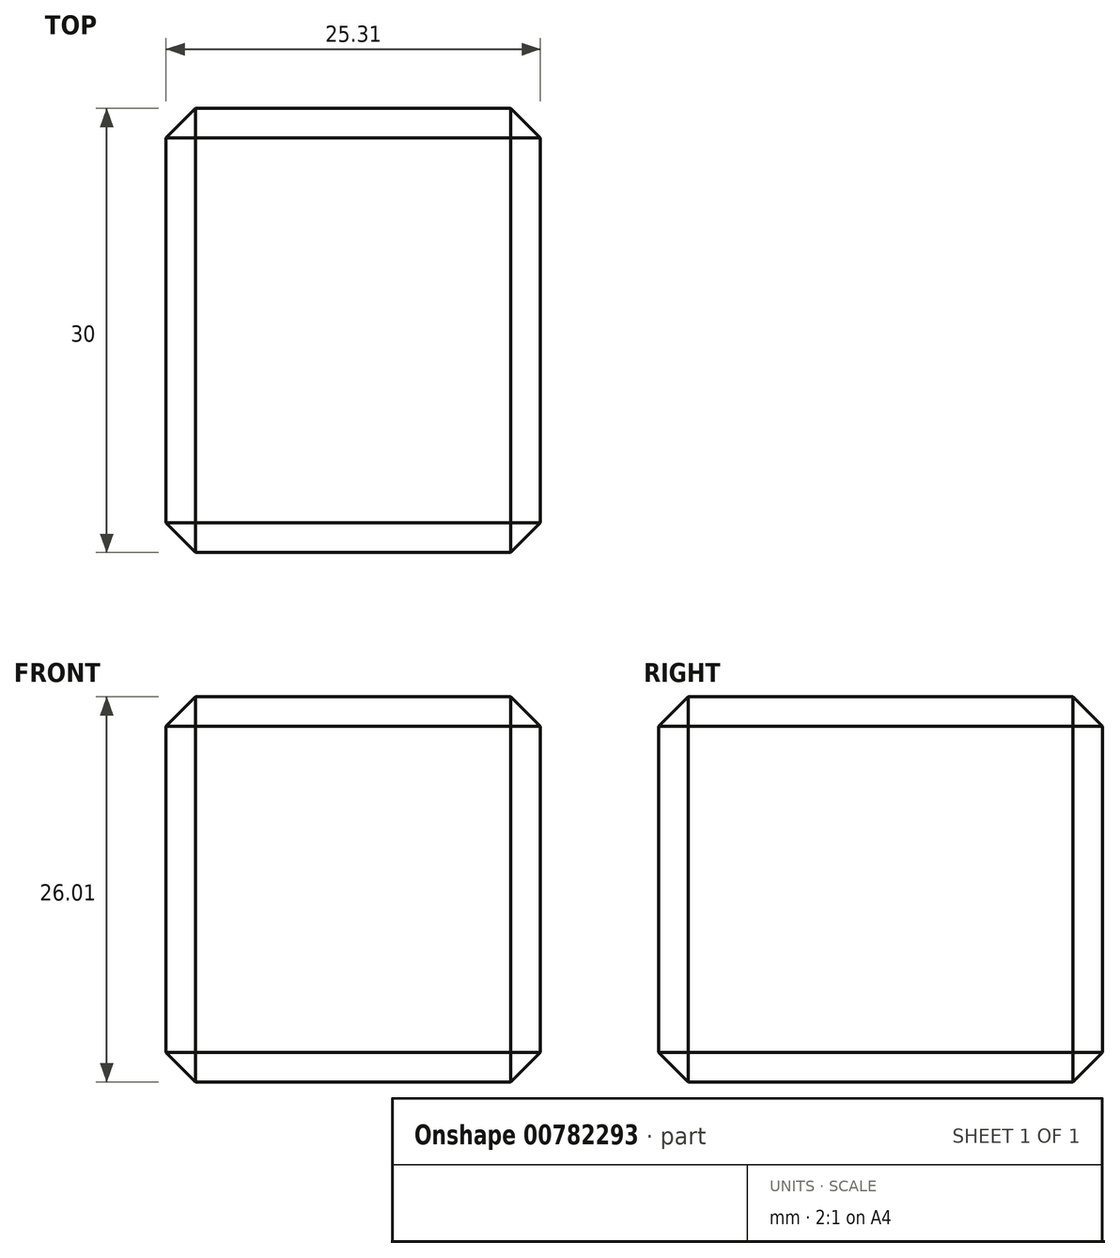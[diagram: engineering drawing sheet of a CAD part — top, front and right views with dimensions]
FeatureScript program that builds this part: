
annotation { "Feature Type Name" : "Feature", "Feature Type Description" : "" }
export const myFeature = defineFeature(function(context is Context, id is Id, definition is map)
    precondition{}
    {
        {
            var Q0;
            Q0=qCreatedBy(makeId("Front.planeOp"),FACE);
            var sketch = newSketch(context, id + "F0", { "sketchPlane" : qUnion([Q0])});
            skLineSegment(sketch, "E0.bottom", {"start": v(0, 0) * mm, "end": v(0, 0) * mm});
            skLineSegment(sketch, "E0.top", {"start": v(0, 0) * mm, "end": v(0, 0) * mm});
            skLineSegment(sketch, "E0.left", {"start": v(0, 0) * mm, "end": v(0, 0) * mm});
            skLineSegment(sketch, "E0.right", {"start": v(0, 0) * mm, "end": v(0, 0) * mm});
            skPoint(sketch, "E0.middle", {"position": v(0, 0) * mm});
            skLineSegment(sketch, "E1.bottom", {"start": v(0, 0) * mm, "end": v(25.31, 0) * mm});
            skLineSegment(sketch, "E1.top", {"start": v(0, 26.01) * mm, "end": v(25.31, 26.01) * mm});
            skLineSegment(sketch, "E1.left", {"start": v(0, 0) * mm, "end": v(0, 26.01) * mm});
            skLineSegment(sketch, "E1.right", {"start": v(25.31, 0) * mm, "end": v(25.31, 26.01) * mm});
            skPoint(sketch, "E1.middle", {"position": v(12.66, 13) * mm});
            skSolve(sketch);
        }
        {
            var Q0;
            Q0=makeQuery(id+"F0.imprint","IMPRINT",FACE,{"disambiguationData":[TD([[makeQuery(id+"F0.imprint","IMPRINT",EDGE,{"derivedFrom":sQuery(id+"F0.wireOp",EDGE,"E1.bottom")}),1.0]])]});
            extrude(context, id + "F1", {"entities" : qUnion([Q0]), "depth" : 30 * mm, "offsetDistance" : 25.4 * mm});
        }
        {
            var Q0;
            Q0=makeQuery(id+"F1.opExtrude","CAP_EDGE",EDGE,{"disambiguationData":[OSD([sQuery(id+"F0.wireOp",EDGE,"E1.right")])],"isStart":true});
            var Q1;
            Q1=makeQuery(id+"F1.opExtrude","CAP_EDGE",EDGE,{"disambiguationData":[OSD([sQuery(id+"F0.wireOp",EDGE,"E1.top")])],"isStart":true});
            var Q2;
            Q2=makeQuery(id+"F1.opExtrude","CAP_EDGE",EDGE,{"disambiguationData":[OSD([sQuery(id+"F0.wireOp",EDGE,"E1.bottom")])],"isStart":true});
            var Q3;
            Q3=makeQuery(id+"F1.opExtrude","CAP_EDGE",EDGE,{"disambiguationData":[OSD([sQuery(id+"F0.wireOp",EDGE,"E1.left")])],"isStart":true});
            var Q4;
            Q4=makeQuery(id+"F1.opExtrude","SWEPT_EDGE",EDGE,{"disambiguationData":[OSD([sQuery(id+"F0.wireOp",EDGE,"E1.top"),sQuery(id+"F0.wireOp",EDGE,"E1.right")])]});
            var Q5;
            Q5=makeQuery(id+"F1.opExtrude","SWEPT_EDGE",EDGE,{"disambiguationData":[OSD([sQuery(id+"F0.wireOp",EDGE,"E1.bottom"),sQuery(id+"F0.wireOp",EDGE,"E1.right")])]});
            var Q6;
            Q6=makeQuery(id+"F1.opExtrude","CAP_EDGE",EDGE,{"disambiguationData":[OSD([sQuery(id+"F0.wireOp",EDGE,"E1.right")])],"isStart":false});
            var Q7;
            Q7=makeQuery(id+"F1.opExtrude","CAP_EDGE",EDGE,{"disambiguationData":[OSD([sQuery(id+"F0.wireOp",EDGE,"E1.top")])],"isStart":false});
            var Q8;
            Q8=makeQuery(id+"F1.opExtrude","SWEPT_EDGE",EDGE,{"disambiguationData":[OSD([sQuery(id+"F0.wireOp",EDGE,"E1.top"),sQuery(id+"F0.wireOp",EDGE,"E1.left")])]});
            var Q9;
            Q9=makeQuery(id+"F1.opExtrude","CAP_EDGE",EDGE,{"disambiguationData":[OSD([sQuery(id+"F0.wireOp",EDGE,"E1.left")])],"isStart":false});
            var Q10;
            Q10=makeQuery(id+"F1.opExtrude","SWEPT_EDGE",EDGE,{"disambiguationData":[OSD([sQuery(id+"F0.wireOp",EDGE,"E1.bottom"),sQuery(id+"F0.wireOp",EDGE,"E1.left")])]});
            var Q11;
            Q11=makeQuery(id+"F1.opExtrude","CAP_EDGE",EDGE,{"disambiguationData":[OSD([sQuery(id+"F0.wireOp",EDGE,"E1.bottom")])],"isStart":false});
            chamfer(context, id + "F2", {"entities" : qUnion([Q0, Q1, Q2, Q3, Q4, Q5, Q6, Q7, Q8, Q9, Q10, Q11]), "width" : 2 * mm, "tangentPropagation" : true});
        }
    });
